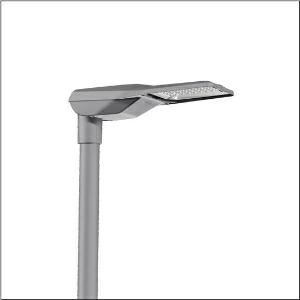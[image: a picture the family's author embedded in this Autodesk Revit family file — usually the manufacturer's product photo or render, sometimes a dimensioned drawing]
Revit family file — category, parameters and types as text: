
# Revit family: streetlight_sl_21_iq_mini___st0_8a_5xe2c41d08hb_7f29
name_source: partatom
category: Lighting Fixtures
units: mm (PartAtom-declared; Revit-internal decimal feet)

## family parameters
Cut with Voids When Loaded = No
Host = Face
Light Source = No
Part Type = Normal
Room Calculation Point = No
Round Connector Dimension = Use Diameter
Shared = No

## types (1)
- --- (1 x LED, 9860 lm, 70.9 W, 4000K)
    Apparent Load = 71 VA
    CIE Flux Codes = 38 75 97 100 100
    Color Rendering = 70
    Color Temperature = 4000K
    Default Elevation = 1800 mm
    Description = Streetlight SL 21 iQ mini, mast luminaire, primary light control with lens, of PMMA, primary optical cover: cover, of toughened safety glass, transparent, light distribution: ST0.8a, light emission: direct distribution, primary light characteristic: asymmetric, installation type: post-top, side-entry, LED, High Power LED, rated luminous flux: 9.860lm, luminous efficacy: 139lm/W, light colour: 740, colour temperature: 4000K, control: Auto-Match, Temp-Guard, Lumen-Switch, Night-Set, Smart-Wire, Light-Fading, Desk-Remote (wireless, voltage-free reading and setting of iQ features in the workshop via application-optimized NFC function/RFID function), optimised constant luminous flux control (CLO 2.0), presetting dimming linear, mains connection: 220..240V, AC, 50/60Hz, start of lifetime: 71W, end of service life: 75W, reduction: 31W, luminaire housing, of diecast aluminium, powder-coated, Siteco® metallic grey (DB 702S), corrosivity category C5 mid according to DIN EN ISO 12944, please order mast flange separately, inclination adjustable: 0°, 5°, 10°, 15°, sealing non-destructively replaceable, multi-level sealing system, length: 628mm, width: 235mm, height: 110mm, mast flange for spigot size: 42mm (side-entry): 5XC10008XM4, 60/48mm (side-entry/post-top): 5XC10108XM2, 76/60mm (side-entry/post-top): 5XC10108XM1, protection rating (complete): IP66, insulation class (complete): insulation class II (safety insulation), certification: CE, ENEC, ENEC+, VDE, impact resistance: IK09, permissible operating ambient temperature for outdoor applications: -40..+50°C, standard-compliant lighting for roads and squares, packaging unit: 1 piece

Light Distribution: ST0.8a
    Height = 110 mm
    Lamp = 1 x LED
    Lamp Light Flux = 9860 lm
    Lamp Power = 70.9 W
    Lamp count = 1
    Length = 625 mm
    Luminous efficacy = 139 lm/W
    Manufacturer = Siteco
    ModVariant = No
    Model = 5XE2C41D08HB
    Number of Poles = 1
    OnlyDefault = Yes
    Power Factor = 1
    Product Name = Streetlight SL 21 iQ mini | ST0.8a
    Product group = mast luminaire | pylon top
    ProductGroupID = 6100
    Protection Class = Protection class II
    Protection Degree = IP 66
    RLX_Detail_Level = 1
    RLX_Emergency_Light_Flux = 0 lm
    RLX_Emergency_Type = 0
    RLX_Emergency_Type_DB = No
    RlxData = <blob elided: 92073 chars, md5=9a8561d9>
    Socket = socket
    Standby Power = 0 W
    System Light Flux = 9860 lm
    System Power = 71 W
    Type Comments = factory setting: luminous flux: 100 % | dim-lin: 254 | 711 mA
    Type Image = l_1003519.jpg
    URL = http://relux.com
    VarID = @adj_107549
    Voltage = 0 V
    Weight = 0.00 kg
    Width = 234 mm

## geometry (parser evidence)
native form markers: Blend x4, Sweep x13
no freeform markers — native parametric forms only
